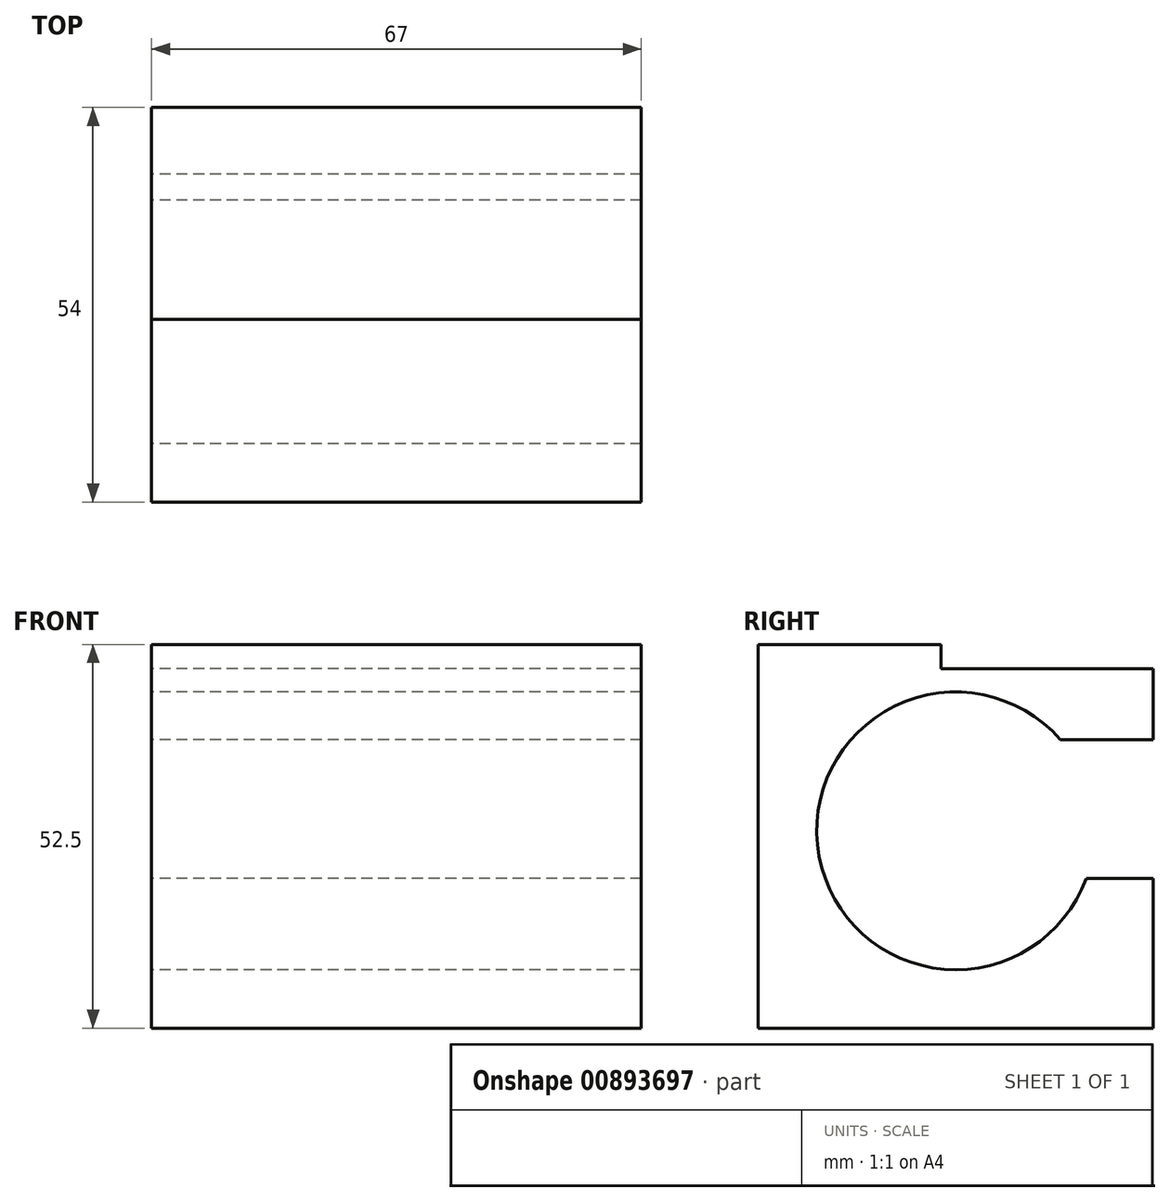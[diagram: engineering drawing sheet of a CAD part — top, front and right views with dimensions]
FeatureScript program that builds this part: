
annotation { "Feature Type Name" : "Feature", "Feature Type Description" : "" }
export const myFeature = defineFeature(function(context is Context, id is Id, definition is map)
    precondition{}
    {
        {
            var Q0;
            Q0=qCreatedBy(makeId("Right.planeOp"),FACE);
            var sketch = newSketch(context, id + "F0", { "sketchPlane" : qUnion([Q0])});
            skLineSegment(sketch, "E0.top", {"start": v(-23.85, -20.5) * mm, "end": v(30.15, -20.5) * mm});
            skCircle(sketch, "E1", {"center": v(3.15, 6.5) * mm, "radius": 19 * mm});
            skLineSegment(sketch, "E2", {"start": v(30.15, 32) * mm, "end": v(1.15, 32) * mm});
            skLineSegment(sketch, "E3", {"start": v(30.15, 28.7) * mm, "end": v(1.15, 28.7) * mm});
            skLineSegment(sketch, "E4", {"start": v(1.15, 32) * mm, "end": v(1.15, 28.7) * mm});
            skLineSegment(sketch, "E5", {"start": v(17.46, 19) * mm, "end": v(30.15, 19) * mm});
            skLineSegment(sketch, "E6", {"start": v(21, 0) * mm, "end": v(30.15, 0) * mm});
            skLineSegment(sketch, "E7", {"start": v(1.15, 32) * mm, "end": v(-23.85, 32) * mm});
            skLineSegment(sketch, "E8", {"start": v(-23.85, 32) * mm, "end": v(-23.85, -20.5) * mm});
            skLineSegment(sketch, "E9", {"start": v(30.15, 28.7) * mm, "end": v(30.15, -20.5) * mm});
            skSolve(sketch);
        }
        {
            var Q0;
            {var subQ7=sQuery(id+"F0.wireOp",EDGE,"E0.bottom");Q0=makeQuery(id+"F0.imprint","IMPRINT",FACE,{"disambiguationData":[TD([[makeQuery(id+"F0.imprint","IMPRINT",EDGE,{"derivedFrom":subQ7}),-1.0]])]});}
            var Q1;
            {var subQ4=sQuery(id+"F0.wireOp",EDGE,"E0.top");Q1=makeQuery(id+"F0.imprint","IMPRINT",FACE,{"disambiguationData":[TD([[makeQuery(id+"F0.imprint","IMPRINT",EDGE,{"derivedFrom":subQ4}),1.0]])]});}
            extrude(context, id + "F1", {"entities" : qUnion([Q0, Q1]), "depth" : 67 * mm, "offsetDistance" : 25 * mm});
        }
    });
